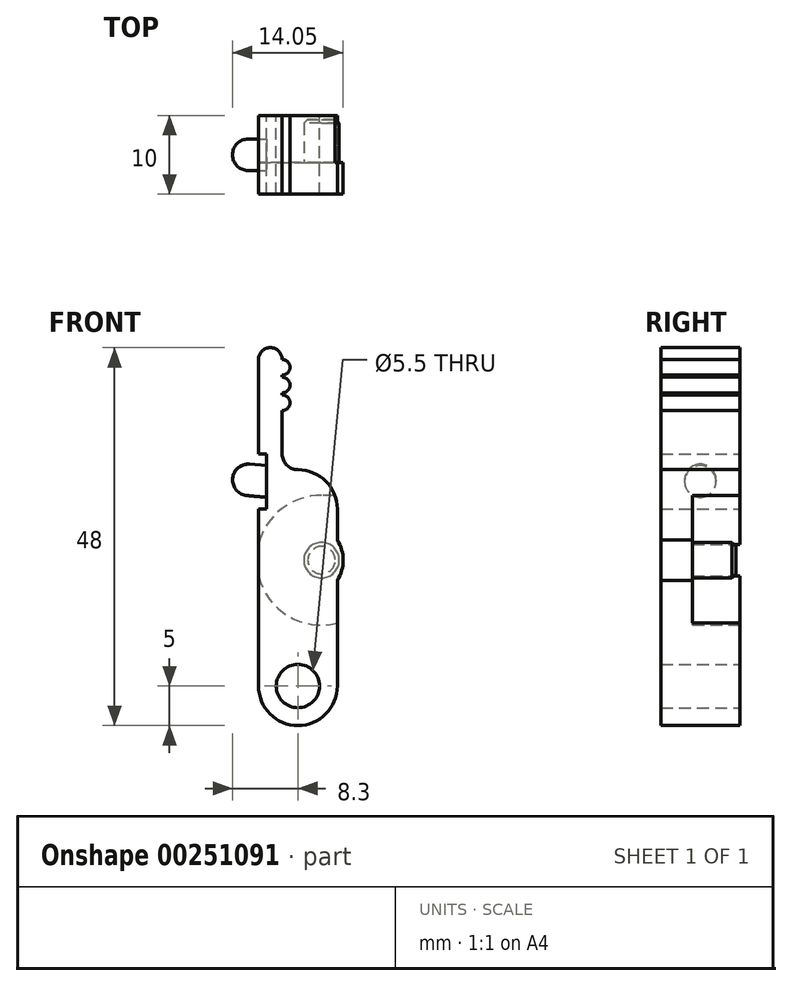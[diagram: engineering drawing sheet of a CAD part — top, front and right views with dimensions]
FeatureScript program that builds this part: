
annotation { "Feature Type Name" : "Feature", "Feature Type Description" : "" }
export const myFeature = defineFeature(function(context is Context, id is Id, definition is map)
    precondition{}
    {
        {
            var Q0;
            Q0=qCreatedBy(makeId("Front.planeOp"),FACE);
            var sketch = newSketch(context, id + "F0", { "sketchPlane" : qUnion([Q0])});
            skLineSegment(sketch, "E0", {"start": v(-5, 41.5) * mm, "end": v(-5, 29.5) * mm});
            skLineSegment(sketch, "E1", {"start": v(-5, 29.5) * mm, "end": v(-4, 29.5) * mm});
            skLineSegment(sketch, "E2", {"start": v(-4, 29.5) * mm, "end": v(-4, 22.5) * mm});
            skLineSegment(sketch, "E3", {"start": v(-4, 22.5) * mm, "end": v(-5, 22.5) * mm});
            skLineSegment(sketch, "E4", {"start": v(-5, 22.5) * mm, "end": v(-5, 0) * mm});
            skLineSegment(sketch, "E5", {"start": v(5, 0) * mm, "end": v(5, 13.44) * mm});
            skLineSegment(sketch, "E6", {"start": v(5, 18.56) * mm, "end": v(5, 27.5) * mm});
            skArc(sketch, "E7", {"start": v(5, 0) * mm, "mid": v(0, -5) * mm, "end": v(-5, 0) * mm});
            skCircle(sketch, "E8", {"center": v(0, 0) * mm, "radius": 2.75 * mm});
            skPoint(sketch, "E9", {"position": v(-4, 26) * mm});
            skArc(sketch, "E10", {"start": v(-5, 41.5) * mm, "mid": v(-3.5, 43) * mm, "end": v(-2, 41.5) * mm});
            skLineSegment(sketch, "E11", {"start": v(-2, 41.5) * mm, "end": v(-2, 29.5) * mm});
            skLineSegment(sketch, "E12", {"start": v(0, 27.5) * mm, "end": v(5, 27.5) * mm});
            skArc(sketch, "E13", {"start": v(-2, 41.5) * mm, "mid": v(-1, 40.5) * mm, "end": v(-2, 39.5) * mm});
            skArc(sketch, "E14.1.0.0", {"start": v(-2, 39.25) * mm, "mid": v(-1, 38.25) * mm, "end": v(-2, 37.25) * mm});
            skArc(sketch, "E14.2.0.0", {"start": v(-2, 37) * mm, "mid": v(-1, 36) * mm, "end": v(-2, 35) * mm});
            skPoint(sketch, "E15.visualSharp", {"position": v(-2, 27.5) * mm});
            skArc(sketch, "E15.filletArc", {"start": v(-2, 29.5) * mm, "mid": v(-1.41, 28.09) * mm, "end": v(0, 27.5) * mm});
            skCircle(sketch, "E16", {"center": v(1, 16) * mm, "radius": 2.75 * mm, "construction": true});
            skArc(sketch, "E17.0", {"start": v(5, 13.44) * mm, "mid": v(5.75, 16) * mm, "end": v(5, 18.56) * mm});
            skCircle(sketch, "E18", {"center": v(1, 16) * mm, "radius": 8 * mm, "construction": true});
            skSolve(sketch);
        }
        {
            var Q0;
            Q0 = qSketchRegion(id + "F0", true);
            extrude(context, id + "F1", {"entities" : qUnion([Q0]), "endBound" : BoundingType.SYMMETRIC, "depth" : 10 * mm});
        }
        {
            var Q0;
            Q0=qCreatedBy(makeId("Front.planeOp"),FACE);
            var sketch = newSketch(context, id + "F2", { "sketchPlane" : qUnion([Q0])});
            skLineSegment(sketch, "E19.0", {"start": v(-4, 29.5) * mm, "end": v(-4, 22.5) * mm, "construction": true});
            skPoint(sketch, "E20", {"position": v(-4, 26) * mm});
            skLineSegment(sketch, "E21", {"start": v(-3.31, 25.94) * mm, "end": v(-4.6, 26.05) * mm, "construction": true});
            skLineSegment(sketch, "E22", {"start": v(-3.14, 27.93) * mm, "end": v(-6.13, 28.2) * mm});
            skArc(sketch, "E23", {"start": v(-6.13, 28.2) * mm, "mid": v(-7.59, 27.73) * mm, "end": v(-8.3, 26.38) * mm});
            skLineSegment(sketch, "E24", {"start": v(-3.14, 27.93) * mm, "end": v(-3.31, 25.94) * mm});
            skLineSegment(sketch, "E25", {"start": v(-8.3, 26.38) * mm, "end": v(-3.31, 25.94) * mm});
            skLineSegment(sketch, "E26.0", {"start": v(-5, 29.5) * mm, "end": v(-4, 29.5) * mm, "construction": true});
            skLineSegment(sketch, "E26.2", {"start": v(-4, 22.5) * mm, "end": v(-5, 22.5) * mm, "construction": true});
            skLineSegment(sketch, "E27", {"start": v(3.32, 26) * mm, "end": v(-13.3, 26) * mm, "construction": true});
            skSolve(sketch);
        }
        {
            var Q0;
            Q0 = qSketchRegion(id + "F2", true);
            var Q1;
            Q1=sQuery(id+"F2.wireOp",EDGE,"E21");
            revolve(context, id + "F3", {"operationType" : NewBodyOperationType.ADD, "entities" : qUnion([Q0]), "axis" : qUnion([Q1]), "revolveType" : RevolveType.FULL});
        }
        {
            var Q0;
            Q0=qCreatedBy(makeId("Right.planeOp"),FACE);
            cPlane(context, id + "F4", {"entities" : qUnion([Q0]), "cplaneType" : CPlaneType.OFFSET, "offset" : 3 * mm, "width" : 150 * mm, "height" : 150 * mm});
        }
        {
            var Q0;
            Q0=qCreatedBy(id+"F4.planeOp",FACE);
            var sketch = newSketch(context, id + "F5", { "sketchPlane" : qUnion([Q0])});
            skLineSegment(sketch, "E28.bottom", {"start": v(5, 24.25) * mm, "end": v(-1, 24.25) * mm});
            skLineSegment(sketch, "E28.top", {"start": v(5, 7.75) * mm, "end": v(-1, 7.75) * mm, "construction": true});
            skLineSegment(sketch, "E28.left", {"start": v(5, 24.25) * mm, "end": v(5, 16) * mm});
            skLineSegment(sketch, "E28.right", {"start": v(-1, 24.25) * mm, "end": v(-1, 16) * mm});
            skPoint(sketch, "E28.middle", {"position": v(2, 16) * mm});
            skLineSegment(sketch, "E29.0", {"start": v(-5, 13.44) * mm, "end": v(5, 13.44) * mm, "construction": true});
            skLineSegment(sketch, "E29.1", {"start": v(-5, 18.56) * mm, "end": v(5, 18.56) * mm, "construction": true});
            skLineSegment(sketch, "E30", {"start": v(0, 18.56) * mm, "end": v(0, 13.44) * mm, "construction": true});
            skPoint(sketch, "E31", {"position": v(0, 16) * mm});
            skLineSegment(sketch, "E32", {"start": v(-5.76, 16) * mm, "end": v(5.86, 16) * mm, "construction": true});
            skLineSegment(sketch, "E33", {"start": v(-1, 16) * mm, "end": v(-1, 7.75) * mm, "construction": true});
            skLineSegment(sketch, "E34", {"start": v(5, 16) * mm, "end": v(5, 7.75) * mm, "construction": true});
            skLineSegment(sketch, "E35", {"start": v(-1, 16) * mm, "end": v(5, 16) * mm});
            skLineSegment(sketch, "E36", {"start": v(2.35, 31.23) * mm, "end": v(2.35, 5.02) * mm, "construction": true});
            skSolve(sketch);
        }
        {
            var Q0;
            Q0 = qSketchRegion(id + "F5", true);
            var Q1;
            Q1=sQuery(id+"F5.wireOp",EDGE,"E32");
            revolve(context, id + "F6", {"operationType" : NewBodyOperationType.REMOVE, "entities" : qUnion([Q0]), "axis" : qUnion([Q1]), "revolveType" : RevolveType.FULL, "oppositeDirection" : true});
        }
        {
            var Q0;
            Q0 = qSketchRegion(id + "F5", true);
            extrude(context, id + "F7", {"entities" : qUnion([Q0]), "operationType" : NewBodyOperationType.REMOVE, "endBound" : BoundingType.THROUGH_ALL, "depth" : 25 * mm});
        }
        {
            var Q0;
            Q0=makeQuery(id+"F1.opExtrude","SWEPT_EDGE",EDGE,{"disambiguationData":[OSD([sQuery(id+"F0.wireOp",EDGE,"E6"),sQuery(id+"F0.wireOp",EDGE,"E12")])]});
            fillet(context, id + "F8", {"entities" : qUnion([Q0]), "radius" : 5 * mm, "tangentPropagation" : true, "allowEdgeOverflow" : false});
        }
        {
            var Q0;
            {var subQ0=sQuery(id+"F5.wireOp",EDGE,"E28.right");Q0=makeQuery(id+"F7.boolean.opBoolean","MERGE",FACE,{"derivedFrom":[makeQuery(id+"F6.boolean.opBoolean","COPY",FACE,{"derivedFrom":makeQuery(id+"F6.opRevolve","SWEPT_FACE",FACE,{"disambiguationData":[OSD([subQ0])]})}),makeQuery(id+"F7.opExtrude","SWEPT_FACE",FACE,{"disambiguationData":[OSD([subQ0])]})]});}
            var sketch = newSketch(context, id + "F9", { "sketchPlane" : qUnion([Q0])});
            skCircle(sketch, "E37", {"center": v(-3, 16) * mm, "radius": 2.25 * mm});
            skSolve(sketch);
        }
        {
            var Q0;
            Q0 = qSketchRegion(id + "F9", true);
            extrude(context, id + "F10", {"entities" : qUnion([Q0]), "operationType" : NewBodyOperationType.ADD, "depth" : 5.5 * mm});
        }
        {
            var Q0;
            Q0=makeQuery(id+"F10.opExtrude","CAP_EDGE",EDGE,{"disambiguationData":[OSD([sQuery(id+"F9.wireOp",EDGE,"E37")])],"isStart":false});
            chamfer(context, id + "F11", {"entities" : qUnion([Q0]), "width" : .5 * mm, "tangentPropagation" : true});
        }
    });
